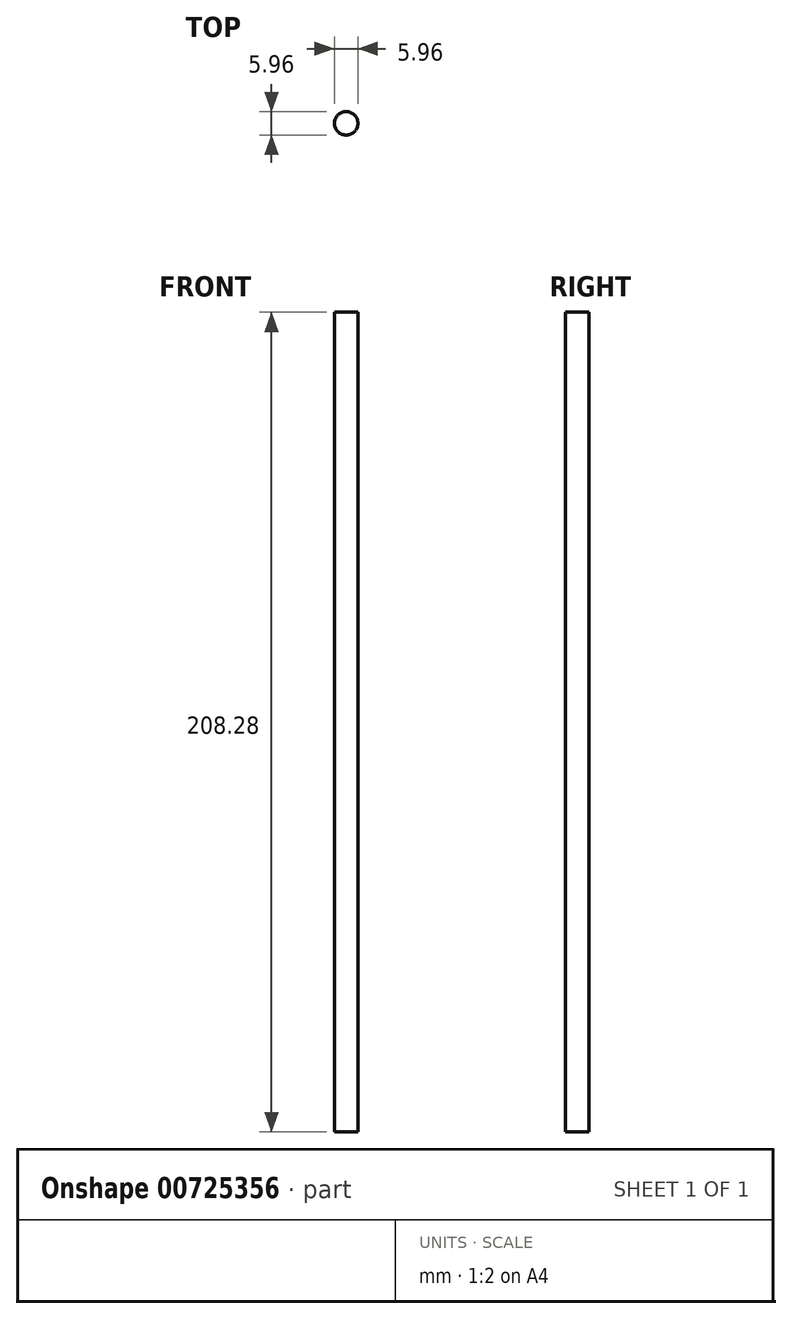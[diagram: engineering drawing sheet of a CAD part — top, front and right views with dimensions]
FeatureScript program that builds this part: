
annotation { "Feature Type Name" : "Feature", "Feature Type Description" : "" }
export const myFeature = defineFeature(function(context is Context, id is Id, definition is map)
    precondition{}
    {
        {
            var Q0;
            Q0=qCreatedBy(makeId("Top.planeOp"),FACE);
            var sketch = newSketch(context, id + "F0", { "sketchPlane" : qUnion([Q0])});
            skCircle(sketch, "E0", {"center": v(0, 0) * mm, "radius": 2.98 * mm});
            skSolve(sketch);
        }
        {
            var Q0;
            Q0 = qSketchRegion(id + "F0", true);
            extrude(context, id + "F1", {"entities" : qUnion([Q0]), "depth" : 208.28 * mm, "offsetDistance" : 25.4 * mm});
        }
    });
